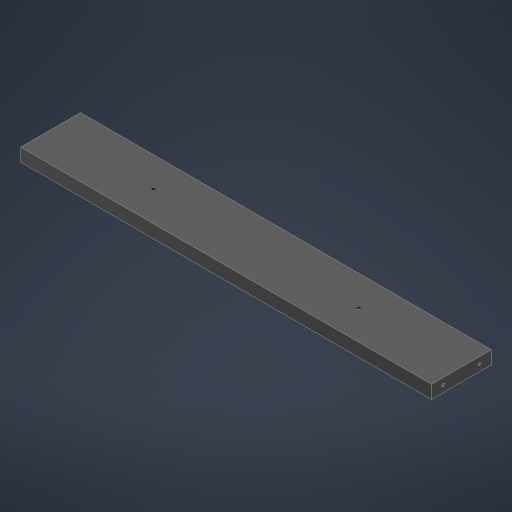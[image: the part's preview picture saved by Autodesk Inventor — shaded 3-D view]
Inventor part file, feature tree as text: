
AUTODESK INVENTOR PART (.ipt)
format: ipt  version: 2024 (Build 280153000, 153)  size: 216,064 bytes
history: native  units: in
note: dims shown in document units (in); Inventor stores cm internally (conversion verified against a paired STEP export)
features: other x1, extrude x1, sketch x1
ambient origin geometry x8: Origin, YZ Plane, XZ Plane, XY Plane, X Axis, Y Axis, Z Axis, Center Point
bodies: Body1 (feature_tree)
feature tree (3):
  other  "Sólido1"
  extrude  "Extrusión1"  Depth=0.0787in
  sketch  "Boceto1"  dims[d0=0.1575in d1=0.1575in d2=0.6299in d3=1.9685in d4=0.7087in d5=0.3543in d6=0.3543in d7=0.0787in d8=0.0in]
